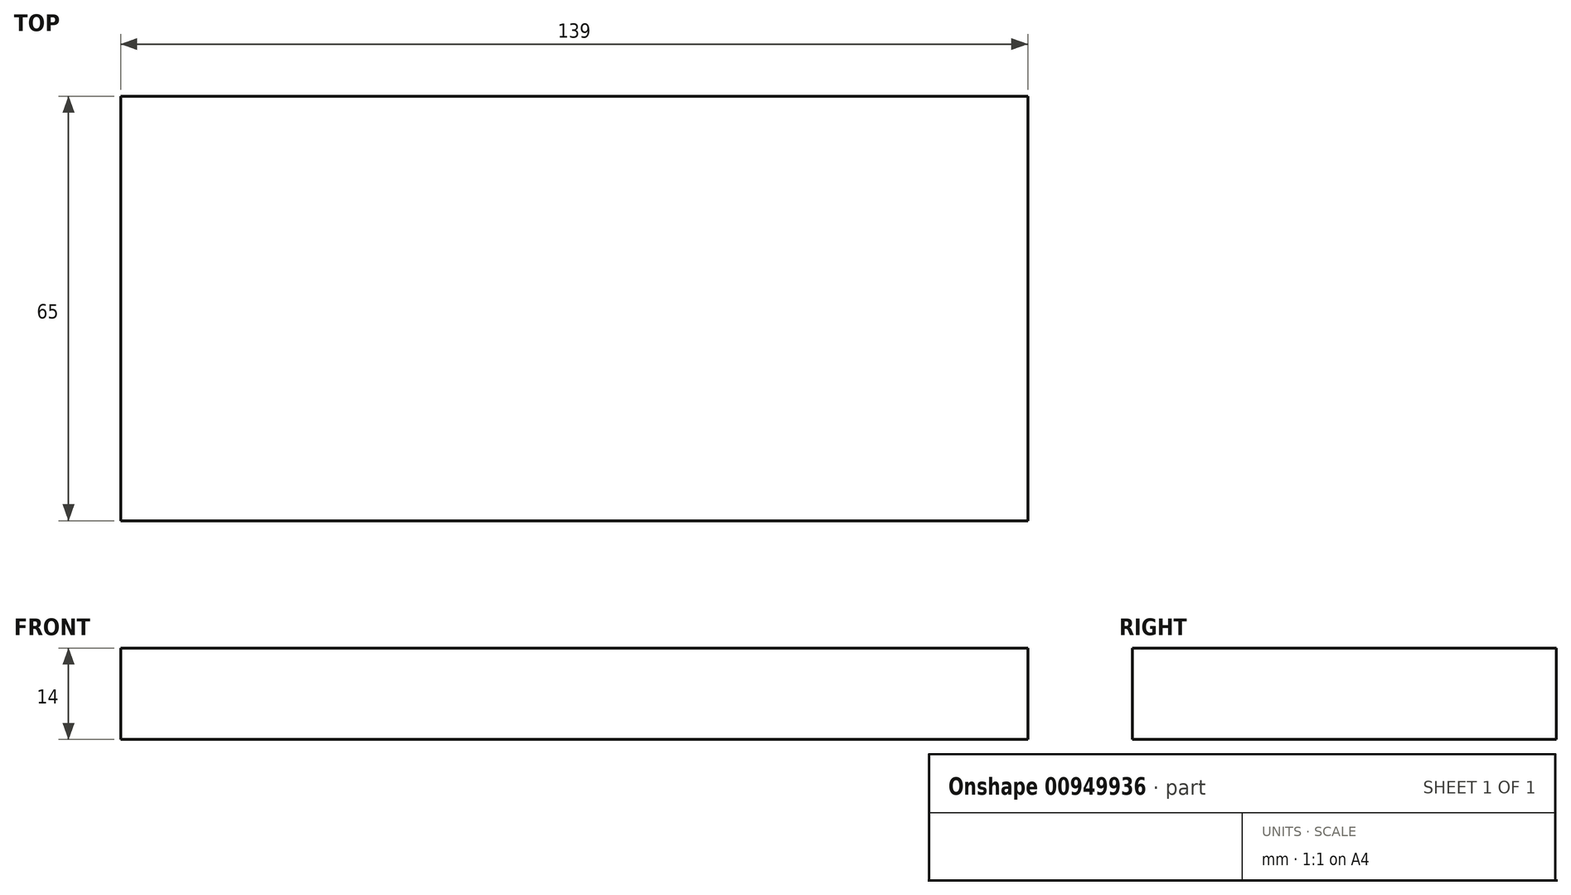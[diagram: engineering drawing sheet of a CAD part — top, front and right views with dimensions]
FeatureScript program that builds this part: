
annotation { "Feature Type Name" : "Feature", "Feature Type Description" : "" }
export const myFeature = defineFeature(function(context is Context, id is Id, definition is map)
    precondition{}
    {
        {
            var Q0;
            Q0=qCreatedBy(makeId("Top.planeOp"),FACE);
            var sketch = newSketch(context, id + "F0", { "sketchPlane" : qUnion([Q0])});
            skLineSegment(sketch, "E0.bottom", {"start": v(69.5, -32.5) * mm, "end": v(-69.5, -32.5) * mm});
            skLineSegment(sketch, "E0.top", {"start": v(69.5, 32.5) * mm, "end": v(-69.5, 32.5) * mm});
            skLineSegment(sketch, "E0.left", {"start": v(69.5, -32.5) * mm, "end": v(69.5, 32.5) * mm});
            skLineSegment(sketch, "E0.right", {"start": v(-69.5, -32.5) * mm, "end": v(-69.5, 32.5) * mm});
            skPoint(sketch, "E0.middle", {"position": v(0, 0) * mm});
            skSolve(sketch);
        }
        {
            var Q0;
            Q0 = qSketchRegion(id + "F0", true);
            extrude(context, id + "F1", {"entities" : qUnion([Q0]), "depth" : 14 * mm, "offsetDistance" : 25 * mm});
        }
    });
